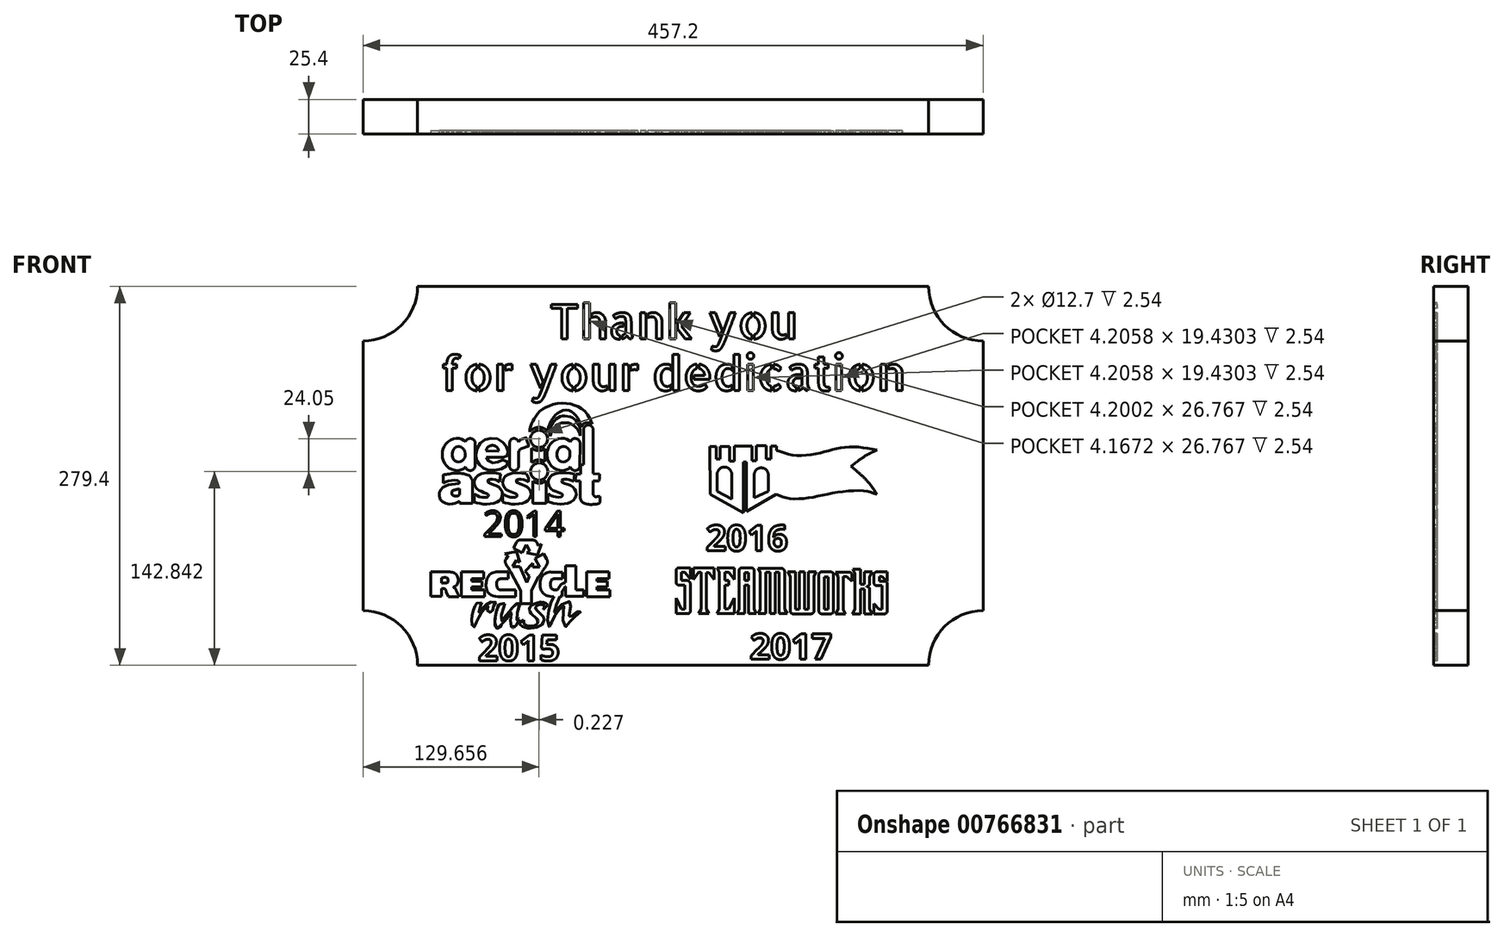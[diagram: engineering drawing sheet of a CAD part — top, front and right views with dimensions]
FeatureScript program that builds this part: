
annotation { "Feature Type Name" : "Feature", "Feature Type Description" : "" }
export const myFeature = defineFeature(function(context is Context, id is Id, definition is map)
    precondition{}
    {
        {
            var Q0;
            Q0=qCreatedBy(makeId("Front.planeOp"),FACE);
            var sketch = newSketch(context, id + "F0", { "sketchPlane" : qUnion([Q0])});
            skLineSegment(sketch, "E0", {"start": v(-457.2, -40.21) * mm, "end": v(-457.2, -239.19) * mm});
            skLineSegment(sketch, "E1", {"start": v(-416.99, -279.4) * mm, "end": v(-40.21, -279.4) * mm});
            skLineSegment(sketch, "E2", {"start": v(0, -239.19) * mm, "end": v(0, -40.21) * mm});
            skLineSegment(sketch, "E3", {"start": v(-40.21, 0) * mm, "end": v(-416.99, 0) * mm});
            skArc(sketch, "E4", {"start": v(-457.2, -40.21) * mm, "mid": v(-428.77, -28.43) * mm, "end": v(-416.99, 0) * mm});
            skLineSegment(sketch, "E5", {"start": v(-228.6, 0) * mm, "end": v(-228.6, -279.4) * mm, "construction": true});
            skLineSegment(sketch, "E6", {"start": v(-457.2, -139.7) * mm, "end": v(0, -139.7) * mm, "construction": true});
            skArc(sketch, "E7.MirrorC", {"start": v(0, -40.21) * mm, "mid": v(-28.43, -28.43) * mm, "end": v(-40.21, 0) * mm});
            skLineSegment(sketch, "E8.MirrorCS", {"start": v(0, -139.7) * mm, "end": v(-457.2, -139.7) * mm, "construction": true});
            skArc(sketch, "E9.MirrorC", {"start": v(-457.2, -239.19) * mm, "mid": v(-428.77, -250.97) * mm, "end": v(-416.99, -279.4) * mm});
            skArc(sketch, "E10.MirrorC", {"start": v(0, -239.19) * mm, "mid": v(-28.43, -250.97) * mm, "end": v(-40.21, -279.4) * mm});
            skSolve(sketch);
        }
        {
            var Q0;
            Q0 = qSketchRegion(id + "F0", true);
            extrude(context, id + "F1", {"entities" : qUnion([Q0]), "depth" : 25.4 * mm, "offsetDistance" : 25.4 * mm});
        }
        {
            var Q0;
            Q0=makeQuery(id+"F1.opExtrude","CAP_FACE",FACE,{"disambiguationData":[OSD([sQuery(id+"F0.wireOp",EDGE,"E0"),sQuery(id+"F0.wireOp",EDGE,"E1"),sQuery(id+"F0.wireOp",EDGE,"E2"),sQuery(id+"F0.wireOp",EDGE,"E3")])],"isStart":false});
            var sketch = newSketch(context, id + "F2", { "sketchPlane" : qUnion([Q0])});
            skFitSpline(sketch, "E11", {"points": [v(-381.64, -114.6) * mm, v(-382.84, -113.47) * mm, v(-384.8, -112.4) * mm, v(-387.44, -111.9) * mm, v(-391.03, -112.52) * mm, v(-394.34, -114.32) * mm, v(-396.64, -116.84) * mm, v(-398.2, -119.8) * mm, v(-398.71, -122.28) * mm, v(-398.65, -125.7) * mm, v(-398.15, -128.16) * mm, v(-396.47, -131.25) * mm, v(-393.66, -133.94) * mm, v(-390.64, -135.45) * mm, v(-386.83, -135.73) * mm, v(-383.74, -134.83) * mm, v(-381.61, -133.04) * mm, v(-379.2, -127.1) * mm], "startDerivative": vector(-26.95, 27.22) * mm, "endDerivative": vector(26.9, 83.07) * mm});
            skArc(sketch, "E12.0.endCap", {"start": v(-374.66, -132.37) * mm, "mid": v(-377.83, -135.83) * mm, "end": v(-381.62, -133.06) * mm});
            skLineSegment(sketch, "E12.0.left", {"start": v(-374.49, -115.92) * mm, "end": v(-374.66, -132.37) * mm});
            skArc(sketch, "E13", {"start": v(-374.49, -115.92) * mm, "mid": v(-377.5, -112.25) * mm, "end": v(-381.64, -114.6) * mm});
            skFitSpline(sketch, "E14", {"points": [v(-387.35, -118.18) * mm, v(-388.71, -118.55) * mm, v(-390.5, -120.1) * mm, v(-391.38, -122.82) * mm, v(-391.33, -125.68) * mm, v(-390.36, -128) * mm, v(-388.57, -129.22) * mm, v(-386.19, -129.42) * mm, v(-383.8, -128.3) * mm, v(-382.45, -126.65) * mm, v(-381.87, -124.26) * mm, v(-382.35, -120.93) * mm, v(-383.66, -119.23) * mm, v(-385.9, -118.26) * mm, v(-387.35, -118.18) * mm]});
            skLineSegment(sketch, "E15", {"start": v(-366.5, -121.42) * mm, "end": v(-357.25, -121.52) * mm});
            skArc(sketch, "E16", {"start": v(-357.25, -121.52) * mm, "mid": v(-361.83, -117.3) * mm, "end": v(-366.5, -121.42) * mm});
            skLineSegment(sketch, "E17", {"start": v(-366.3, -126.1) * mm, "end": v(-353.65, -126.1) * mm});
            skFitSpline(sketch, "E18", {"points": [v(-353.65, -126.1) * mm, v(-351.29, -125.6) * mm, v(-350.5, -124.26) * mm, v(-350.32, -121.14) * mm, v(-351.15, -118.92) * mm, v(-352.54, -116.7) * mm, v(-354.94, -114.3) * mm, v(-358.36, -112.36) * mm, v(-362.43, -112) * mm, v(-366.58, -112.92) * mm, v(-369.54, -114.58) * mm, v(-372.13, -117.35) * mm, v(-373.6, -121.14) * mm, v(-374.01, -124.8) * mm, v(-373.49, -127.83) * mm, v(-371.99, -130.8) * mm, v(-370, -132.86) * mm, v(-367.62, -134.4) * mm, v(-364.3, -135.57) * mm, v(-359.6, -135.7) * mm, v(-355.24, -134.72) * mm, v(-351.99, -132.9) * mm, v(-350.55, -131.34) * mm, v(-350.81, -129.12) * mm, v(-353.65, -127.95) * mm, v(-356.55, -129) * mm, v(-359.22, -130.03) * mm, v(-362.02, -130.1) * mm, v(-364.3, -129.06) * mm, v(-365.67, -127.75) * mm, v(-366.3, -126.1) * mm], "startDerivative": vector(116.89, 0) * mm, "endDerivative": vector(-21.57, 62.43) * mm});
            skArc(sketch, "E19.0.startCap", {"start": v(-349.14, -115.47) * mm, "mid": v(-346.25, -112.2) * mm, "end": v(-342.64, -114.66) * mm});
            skArc(sketch, "E19.0.endCap", {"start": v(-342.54, -132.58) * mm, "mid": v(-345.84, -135.88) * mm, "end": v(-349.14, -132.58) * mm});
            skLineSegment(sketch, "E19.0.left", {"start": v(-342.54, -122.14) * mm, "end": v(-342.54, -132.58) * mm});
            skLineSegment(sketch, "E19.0.right", {"start": v(-349.14, -115.47) * mm, "end": v(-349.14, -132.58) * mm});
            skFitSpline(sketch, "E20", {"points": [v(-342.64, -114.66) * mm, v(-340.58, -112.8) * mm, v(-338.46, -112.1) * mm, v(-336.5, -111.86) * mm, v(-336.5, -113.74) * mm, v(-335, -117.27) * mm, v(-335.4, -117.98) * mm, v(-336.81, -118.37) * mm, v(-338.54, -118.92) * mm, v(-341.05, -119.86) * mm, v(-342.54, -122.14) * mm], "startDerivative": vector(17.8, 19.08) * mm, "endDerivative": vector(-10.39, -23.26) * mm});
            skCircle(sketch, "E21", {"center": v(-327.54, -112.5) * mm, "radius": 6.35 * mm});
            skArc(sketch, "E22", {"start": v(-332.85, -119.24) * mm, "mid": v(-328.08, -121.06) * mm, "end": v(-323.11, -119.84) * mm});
            skFitSpline(sketch, "E23", {"points": [v(-334.25, -107.17) * mm, v(-334.19, -104.93) * mm, v(-333.33, -102.43) * mm, v(-332.32, -99.94) * mm, v(-331.24, -97.7) * mm, v(-329.36, -95.3) * mm, v(-327.13, -92.47) * mm, v(-323.79, -89.99) * mm, v(-319.93, -88.1) * mm, v(-313.59, -86.39) * mm, v(-306.99, -86.39) * mm, v(-301.59, -87.41) * mm, v(-296.7, -89.9) * mm, v(-292.24, -93.67) * mm, v(-288.04, -101.47) * mm], "startDerivative": vector(-2.37, 43.6) * mm, "endDerivative": vector(38.1, -85.11) * mm});
            skFitSpline(sketch, "E24", {"points": [v(-288.04, -101.47) * mm, v(-290.36, -100.61) * mm, v(-292.59, -100.7) * mm, v(-294.99, -101.47) * mm, v(-296.2, -103.49) * mm, v(-297.5, -99.8) * mm, v(-299.73, -95.99) * mm, v(-302.19, -93.41) * mm, v(-305.1, -91.61) * mm, v(-308.96, -91.44) * mm, v(-313.07, -93.07) * mm, v(-316.5, -96.16) * mm, v(-319.59, -101.47) * mm, v(-321.36, -106.57) * mm], "startDerivative": vector(-37.27, 17.9) * mm, "endDerivative": vector(-16.52, -54.42) * mm});
            skCircle(sketch, "E25", {"center": v(-327.32, -136.56) * mm, "radius": 6.35 * mm});
            skArc(sketch, "E26", {"start": v(-332.15, -143.64) * mm, "mid": v(-327.13, -145.13) * mm, "end": v(-322.18, -143.42) * mm});
            skLineSegment(sketch, "E27", {"start": v(-332.85, -119.24) * mm, "end": v(-332.85, -130.01) * mm});
            skLineSegment(sketch, "E28", {"start": v(-323.11, -119.84) * mm, "end": v(-323.11, -129.09) * mm});
            skArc(sketch, "E29.trimOffspring", {"start": v(-321.36, -106.57) * mm, "mid": v(-327.94, -103.94) * mm, "end": v(-334.25, -107.17) * mm});
            skLineSegment(sketch, "E30", {"start": v(-332.15, -143.64) * mm, "end": v(-332.15, -159.4) * mm});
            skLineSegment(sketch, "E31", {"start": v(-331.52, -160.03) * mm, "end": v(-322.83, -160.12) * mm});
            skLineSegment(sketch, "E32", {"start": v(-322.18, -159.49) * mm, "end": v(-322.18, -143.42) * mm});
            skPoint(sketch, "E33.visualSharp", {"position": v(-332.15, -160.02) * mm});
            skArc(sketch, "E33.filletArc", {"start": v(-332.15, -159.4) * mm, "mid": v(-331.96, -159.84) * mm, "end": v(-331.52, -160.03) * mm});
            skPoint(sketch, "E34.visualSharp", {"position": v(-322.18, -160.13) * mm});
            skArc(sketch, "E34.filletArc", {"start": v(-322.83, -160.12) * mm, "mid": v(-322.37, -159.94) * mm, "end": v(-322.18, -159.49) * mm});
            skArc(sketch, "E35.trimOffspring", {"start": v(-323.11, -129.09) * mm, "mid": v(-328.13, -128.02) * mm, "end": v(-332.85, -130.01) * mm});
            skFitSpline(sketch, "E36", {"points": [v(-319.18, -110.39) * mm, v(-319.6, -107.16) * mm, v(-318.85, -103.4) * mm, v(-316.92, -100.19) * mm, v(-314.67, -97.72) * mm, v(-311.66, -95.9) * mm, v(-308, -95.57) * mm, v(-303.93, -96.32) * mm, v(-301.25, -97.93) * mm, v(-299.2, -100.5) * mm, v(-297.27, -104.8) * mm, v(-297.17, -110.17) * mm], "startDerivative": vector(-7.7, 37.27) * mm, "endDerivative": vector(-3.75, -50.87) * mm});
            skFitSpline(sketch, "E37", {"points": [v(-297.17, -110.17) * mm, v(-298.35, -106.52) * mm, v(-299.74, -104.48) * mm, v(-302.21, -102.33) * mm, v(-305.22, -100.83) * mm, v(-308.55, -100.61) * mm, v(-311.88, -101.04) * mm, v(-316.06, -103.84) * mm, v(-317.89, -106.63) * mm, v(-319.18, -110.39) * mm], "startDerivative": vector(-9.3, 34.22) * mm, "endDerivative": vector(-10.28, -33.52) * mm});
            skFitSpline(sketch, "E38", {"points": [v(-304.35, -114.6) * mm, v(-305.55, -113.47) * mm, v(-307.5, -112.4) * mm, v(-310.14, -111.9) * mm, v(-313.73, -112.52) * mm, v(-317.04, -114.32) * mm, v(-319.34, -116.84) * mm, v(-320.9, -119.8) * mm, v(-321.41, -122.28) * mm, v(-321.36, -125.7) * mm, v(-320.85, -128.16) * mm, v(-319.17, -131.25) * mm, v(-316.37, -133.94) * mm, v(-313.34, -135.45) * mm, v(-309.53, -135.73) * mm, v(-306.44, -134.83) * mm, v(-304.31, -133.04) * mm, v(-301.9, -127.1) * mm], "startDerivative": vector(-26.95, 27.22) * mm, "endDerivative": vector(26.9, 83.07) * mm});
            skArc(sketch, "E39.0.endCap", {"start": v(-297.37, -132.37) * mm, "mid": v(-300.54, -135.83) * mm, "end": v(-304.33, -133.06) * mm});
            skLineSegment(sketch, "E39.0.left", {"start": v(-297.2, -115.92) * mm, "end": v(-297.37, -132.37) * mm});
            skArc(sketch, "E40", {"start": v(-297.2, -115.92) * mm, "mid": v(-300.21, -112.25) * mm, "end": v(-304.35, -114.6) * mm});
            skFitSpline(sketch, "E41", {"points": [v(-310.05, -118.18) * mm, v(-311.41, -118.55) * mm, v(-313.2, -120.1) * mm, v(-314.08, -122.82) * mm, v(-314.03, -125.68) * mm, v(-313.06, -128) * mm, v(-311.27, -129.22) * mm, v(-308.9, -129.42) * mm, v(-306.51, -128.3) * mm, v(-305.15, -126.65) * mm, v(-304.57, -124.26) * mm, v(-305.06, -120.93) * mm, v(-306.37, -119.23) * mm, v(-308.6, -118.26) * mm, v(-310.05, -118.18) * mm]});
            skLineSegment(sketch, "E42", {"start": v(-287.66, -105.14) * mm, "end": v(-287.66, -138.24) * mm});
            skLineSegment(sketch, "E43", {"start": v(-287.66, -138.24) * mm, "end": v(-282.77, -138.3) * mm});
            skLineSegment(sketch, "E44", {"start": v(-282.77, -138.3) * mm, "end": v(-282.77, -141.77) * mm});
            skLineSegment(sketch, "E45", {"start": v(-282.77, -141.77) * mm, "end": v(-283.27, -143.55) * mm});
            skLineSegment(sketch, "E46", {"start": v(-283.27, -143.55) * mm, "end": v(-287.52, -143.5) * mm});
            skLineSegment(sketch, "E47", {"start": v(-287.52, -143.5) * mm, "end": v(-287.52, -153.4) * mm});
            skFitSpline(sketch, "E48", {"points": [v(-287.52, -153.4) * mm, v(-286.84, -154.57) * mm, v(-285.76, -155.2) * mm, v(-283.67, -154.8) * mm], "startDerivative": vector(1.89, -4.02) * mm, "endDerivative": vector(5.77, 1.79) * mm});
            skLineSegment(sketch, "E49", {"start": v(-283.67, -154.8) * mm, "end": v(-282.48, -154.8) * mm});
            skLineSegment(sketch, "E50", {"start": v(-282.48, -154.8) * mm, "end": v(-282.48, -157.52) * mm});
            skFitSpline(sketch, "E51", {"points": [v(-282.48, -157.52) * mm, v(-282.48, -159.3) * mm, v(-283.82, -160.44) * mm, v(-286.32, -160.54) * mm, v(-289.34, -160.96) * mm, v(-291.43, -160.65) * mm, v(-293.82, -160.02) * mm, v(-296.74, -157.52) * mm, v(-297.16, -154.08) * mm, v(-297.05, -143.67) * mm], "startDerivative": vector(3.8, -22.5) * mm, "endDerivative": vector(0.14, 58.8) * mm});
            skLineSegment(sketch, "E52", {"start": v(-297.05, -143.67) * mm, "end": v(-300.6, -143.67) * mm});
            skLineSegment(sketch, "E53", {"start": v(-300.6, -143.67) * mm, "end": v(-300.13, -138.49) * mm});
            skLineSegment(sketch, "E54", {"start": v(-300.13, -138.49) * mm, "end": v(-296.71, -138.49) * mm});
            skLineSegment(sketch, "E55", {"start": v(-296.71, -138.49) * mm, "end": v(-296.71, -132.98) * mm});
            skArc(sketch, "E56", {"start": v(-295.25, -131.44) * mm, "mid": v(-296.29, -131.92) * mm, "end": v(-296.71, -132.98) * mm});
            skLineSegment(sketch, "E57", {"start": v(-295.25, -131.44) * mm, "end": v(-294.5, -131.4) * mm});
            skLineSegment(sketch, "E58", {"start": v(-294.5, -131.4) * mm, "end": v(-294.5, -105.14) * mm});
            skArc(sketch, "E59", {"start": v(-287.66, -105.14) * mm, "mid": v(-291.08, -102.23) * mm, "end": v(-294.5, -105.14) * mm});
            skLineSegment(sketch, "E60", {"start": v(-398.2, -144.95) * mm, "end": v(-398.2, -139.97) * mm});
            skFitSpline(sketch, "E61", {"points": [v(-398.2, -139.97) * mm, v(-398.2, -139.26) * mm, v(-395.87, -138.75) * mm, v(-392.12, -138.03) * mm, v(-387.72, -137.9) * mm, v(-384.23, -137.97) * mm, v(-381.32, -138.62) * mm, v(-378.47, -139.97) * mm, v(-376.61, -143.08) * mm], "startDerivative": vector(-3.73, 12.95) * mm, "endDerivative": vector(10.17, -25.55) * mm});
            skLineSegment(sketch, "E62", {"start": v(-376.61, -143.08) * mm, "end": v(-376.61, -160.06) * mm});
            skLineSegment(sketch, "E63", {"start": v(-376.61, -160.06) * mm, "end": v(-386.1, -160.06) * mm});
            skLineSegment(sketch, "E64", {"start": v(-386.1, -160.06) * mm, "end": v(-386.1, -158.47) * mm});
            skFitSpline(sketch, "E65", {"points": [v(-386.1, -158.47) * mm, v(-388.17, -159.47) * mm, v(-389.68, -160) * mm, v(-391.5, -160.44) * mm, v(-395.28, -160.28) * mm, v(-399.09, -158.47) * mm, v(-400.85, -155.44) * mm, v(-400.85, -151.7) * mm, v(-399.3, -149.22) * mm, v(-396.75, -147.39) * mm, v(-393.67, -146.36) * mm, v(-390, -145.78) * mm, v(-386.1, -145.12) * mm, v(-386.1, -144.31) * mm, v(-387.23, -143.29) * mm, v(-390.23, -143.07) * mm, v(-392.94, -143.43) * mm, v(-395.72, -144.1) * mm, v(-398.2, -144.95) * mm], "startDerivative": vector(-42.37, -21.84) * mm, "endDerivative": vector(-44.8, -16.78) * mm});
            skLineSegment(sketch, "E66", {"start": v(-386.13, -149.22) * mm, "end": v(-386.13, -153.69) * mm});
            skFitSpline(sketch, "E67", {"points": [v(-386.13, -153.69) * mm, v(-387.15, -154.35) * mm, v(-388.4, -154.71) * mm, v(-390, -154.64) * mm, v(-391.47, -153.69) * mm, v(-391.86, -152.33) * mm, v(-391.42, -150.88) * mm, v(-390, -150.17) * mm, v(-388.03, -149.8) * mm, v(-386.13, -149.22) * mm], "startDerivative": vector(-10.07, -7.34) * mm, "endDerivative": vector(14.7, 5.52) * mm});
            skLineSegment(sketch, "E68", {"start": v(-355.88, -138.5) * mm, "end": v(-356.38, -144.04) * mm});
            skLineSegment(sketch, "E69", {"start": v(-375.3, -153.7) * mm, "end": v(-375.35, -158.95) * mm});
            skFitSpline(sketch, "E70", {"points": [v(-375.3, -153.7) * mm, v(-375.01, -153.46) * mm, v(-374.4, -153.36) * mm, v(-373.52, -154.01) * mm, v(-371.66, -154.98) * mm, v(-370.04, -155.4) * mm, v(-368.18, -155.71) * mm, v(-366.04, -155.58) * mm, v(-365.07, -155.08) * mm, v(-364.6, -154.25) * mm, v(-364.97, -153.33) * mm, v(-365.7, -152.89) * mm, v(-366.98, -152.39) * mm, v(-368.73, -151.73) * mm, v(-370.12, -151.16) * mm, v(-372.19, -150.3) * mm, v(-373.73, -148.8) * mm, v(-374.88, -146.84) * mm, v(-375.3, -144.62) * mm, v(-374.45, -141.62) * mm, v(-372.3, -139.3) * mm, v(-368.1, -137.83) * mm, v(-360.72, -137.7) * mm, v(-355.88, -138.5) * mm], "startDerivative": vector(12.94, 13.12) * mm, "endDerivative": vector(65.15, -13.59) * mm});
            skFitSpline(sketch, "E71", {"points": [v(-356.38, -144.04) * mm, v(-357.93, -143.41) * mm, v(-359.6, -142.7) * mm, v(-361.14, -142.36) * mm, v(-363.24, -142.36) * mm, v(-364.88, -142.89) * mm, v(-365.4, -144.04) * mm, v(-364.3, -145.05) * mm, v(-361.47, -146.04) * mm, v(-359.6, -146.69) * mm, v(-357.4, -147.8) * mm, v(-355.88, -149.38) * mm, v(-354.78, -151.16) * mm, v(-354.52, -154.17) * mm, v(-355.88, -157.2) * mm, v(-357.66, -158.7) * mm, v(-360.16, -159.88) * mm, v(-363.77, -160.54) * mm, v(-367.18, -160.8) * mm, v(-370.6, -160.21) * mm, v(-373.15, -159.69) * mm, v(-375.35, -158.95) * mm], "startDerivative": vector(-38, 14.53) * mm, "endDerivative": vector(-45.82, 17.03) * mm});
            skLineSegment(sketch, "E72", {"start": v(-335.08, -141.26) * mm, "end": v(-335.33, -144.03) * mm});
            skLineSegment(sketch, "E73", {"start": v(-354.25, -153.7) * mm, "end": v(-354.3, -158.95) * mm});
            skFitSpline(sketch, "E74", {"points": [v(-354.25, -153.7) * mm, v(-353.96, -153.46) * mm, v(-353.36, -153.36) * mm, v(-352.47, -154.01) * mm, v(-350.61, -154.98) * mm, v(-349, -155.4) * mm, v(-347.14, -155.71) * mm, v(-345, -155.58) * mm, v(-344.02, -155.08) * mm, v(-343.55, -154.25) * mm, v(-343.92, -153.33) * mm, v(-344.65, -152.89) * mm, v(-345.93, -152.39) * mm, v(-347.68, -151.73) * mm, v(-349.07, -151.16) * mm, v(-351.14, -150.3) * mm, v(-352.68, -148.8) * mm, v(-353.83, -146.84) * mm, v(-354.25, -144.62) * mm, v(-353.4, -141.62) * mm, v(-351.26, -139.3) * mm, v(-347.04, -137.83) * mm, v(-339.67, -137.7) * mm, v(-334.83, -138.5) * mm], "startDerivative": vector(12.94, 13.12) * mm, "endDerivative": vector(65.15, -13.59) * mm});
            skFitSpline(sketch, "E75", {"points": [v(-335.33, -144.03) * mm, v(-336.88, -143.41) * mm, v(-338.56, -142.7) * mm, v(-340.1, -142.36) * mm, v(-342.2, -142.36) * mm, v(-343.83, -142.89) * mm, v(-344.36, -144.03) * mm, v(-343.25, -145.05) * mm, v(-340.42, -146.04) * mm, v(-338.56, -146.69) * mm, v(-336.35, -147.8) * mm, v(-334.83, -149.38) * mm, v(-333.73, -151.16) * mm, v(-333.47, -154.17) * mm, v(-334.83, -157.2) * mm, v(-336.62, -158.7) * mm, v(-339.1, -159.88) * mm, v(-342.72, -160.54) * mm, v(-346.13, -160.8) * mm, v(-349.54, -160.21) * mm, v(-352.1, -159.69) * mm, v(-354.3, -158.95) * mm], "startDerivative": vector(-38, 14.53) * mm, "endDerivative": vector(-45.82, 17.03) * mm});
            skLineSegment(sketch, "E76", {"start": v(-335.08, -141.26) * mm, "end": v(-336.71, -138.11) * mm});
            skPoint(sketch, "E77.orphan", {"position": v(-334.83, -138.49) * mm});
            skLineSegment(sketch, "E78", {"start": v(-301.37, -138.37) * mm, "end": v(-301.87, -143.92) * mm});
            skLineSegment(sketch, "E79", {"start": v(-320.8, -153.58) * mm, "end": v(-320.85, -158.84) * mm});
            skFitSpline(sketch, "E80", {"points": [v(-320.8, -153.58) * mm, v(-320.5, -153.34) * mm, v(-319.9, -153.24) * mm, v(-319.02, -153.9) * mm, v(-317.16, -154.86) * mm, v(-315.54, -155.28) * mm, v(-313.68, -155.6) * mm, v(-311.53, -155.46) * mm, v(-310.57, -154.97) * mm, v(-310.1, -154.13) * mm, v(-310.46, -153.21) * mm, v(-311.2, -152.77) * mm, v(-312.48, -152.27) * mm, v(-314.23, -151.62) * mm, v(-315.61, -151.04) * mm, v(-317.68, -150.18) * mm, v(-319.22, -148.69) * mm, v(-320.38, -146.73) * mm, v(-320.8, -144.5) * mm, v(-319.95, -141.5) * mm, v(-317.8, -139.18) * mm, v(-313.59, -137.72) * mm, v(-306.22, -137.58) * mm, v(-301.37, -138.37) * mm], "startDerivative": vector(12.94, 13.12) * mm, "endDerivative": vector(65.15, -13.59) * mm});
            skFitSpline(sketch, "E81", {"points": [v(-301.87, -143.92) * mm, v(-303.42, -143.3) * mm, v(-305.1, -142.58) * mm, v(-306.64, -142.25) * mm, v(-308.74, -142.25) * mm, v(-310.38, -142.77) * mm, v(-310.9, -143.92) * mm, v(-309.8, -144.94) * mm, v(-306.97, -145.92) * mm, v(-305.1, -146.57) * mm, v(-302.9, -147.7) * mm, v(-301.37, -149.27) * mm, v(-300.27, -151.04) * mm, v(-300.01, -154.06) * mm, v(-301.37, -157.08) * mm, v(-303.16, -158.59) * mm, v(-305.65, -159.77) * mm, v(-309.26, -160.42) * mm, v(-312.68, -160.69) * mm, v(-316.09, -160.1) * mm, v(-318.65, -159.57) * mm, v(-320.85, -158.84) * mm], "startDerivative": vector(-38, 14.53) * mm, "endDerivative": vector(-45.82, 17.03) * mm});
            skLineSegment(sketch, "E82", {"start": v(-384.8, -210.42) * mm, "end": v(-384.8, -228.88) * mm});
            skLineSegment(sketch, "E83", {"start": v(-384.8, -228.88) * mm, "end": v(-367.7, -228.88) * mm});
            skLineSegment(sketch, "E84", {"start": v(-367.7, -228.88) * mm, "end": v(-367.7, -223.75) * mm});
            skLineSegment(sketch, "E85", {"start": v(-367.7, -223.75) * mm, "end": v(-377.03, -223.75) * mm});
            skLineSegment(sketch, "E86", {"start": v(-377.03, -223.75) * mm, "end": v(-377.03, -221.76) * mm});
            skLineSegment(sketch, "E87", {"start": v(-377.03, -221.76) * mm, "end": v(-369.54, -221.76) * mm});
            skLineSegment(sketch, "E88", {"start": v(-369.54, -221.76) * mm, "end": v(-369.54, -217.59) * mm});
            skLineSegment(sketch, "E89", {"start": v(-369.54, -217.59) * mm, "end": v(-377.1, -217.59) * mm});
            skLineSegment(sketch, "E90", {"start": v(-377.1, -217.59) * mm, "end": v(-377.1, -215.6) * mm});
            skLineSegment(sketch, "E91", {"start": v(-377.1, -215.6) * mm, "end": v(-368.11, -215.6) * mm});
            skLineSegment(sketch, "E92", {"start": v(-368.11, -215.6) * mm, "end": v(-368.11, -210.42) * mm});
            skLineSegment(sketch, "E93", {"start": v(-368.11, -210.42) * mm, "end": v(-384.8, -210.42) * mm});
            skLineSegment(sketch, "E94.bottom", {"start": v(-407.17, -210.59) * mm, "end": v(-399.46, -210.59) * mm});
            skLineSegment(sketch, "E94.top", {"start": v(-407.17, -228.77) * mm, "end": v(-399.46, -228.77) * mm});
            skLineSegment(sketch, "E94.left", {"start": v(-407.17, -210.59) * mm, "end": v(-407.17, -228.77) * mm});
            skLineSegment(sketch, "E94.right", {"start": v(-399.46, -214.93) * mm, "end": v(-399.46, -218.85) * mm});
            skFitSpline(sketch, "E95", {"points": [v(-399.46, -210.59) * mm, v(-394.1, -210.59) * mm, v(-391.95, -210.85) * mm, v(-390.32, -211.33) * mm, v(-388.8, -212.13) * mm, v(-387.86, -213.28) * mm, v(-387.32, -214.43) * mm, v(-387.1, -216.02) * mm, v(-387.13, -217.71) * mm, v(-387.52, -219.17) * mm, v(-388.32, -220.4) * mm, v(-389.7, -221.48) * mm, v(-390.8, -221.9) * mm], "startDerivative": vector(42.38, 0.73) * mm, "endDerivative": vector(-16, -4.77) * mm});
            skFitSpline(sketch, "E96", {"points": [v(-390.8, -221.9) * mm, v(-390.05, -222.32) * mm, v(-389.1, -223.07) * mm, v(-388.37, -224.46) * mm, v(-387.86, -225.6) * mm, v(-386.56, -228.88) * mm], "startDerivative": vector(4.88, -2.66) * mm, "endDerivative": vector(4.84, -12.6) * mm});
            skLineSegment(sketch, "E97", {"start": v(-386.56, -228.88) * mm, "end": v(-394.38, -228.88) * mm});
            skLineSegment(sketch, "E98", {"start": v(-394.38, -228.88) * mm, "end": v(-395.7, -225.57) * mm});
            skFitSpline(sketch, "E99", {"points": [v(-395.7, -225.57) * mm, v(-396.16, -224.31) * mm, v(-396.58, -223.37) * mm, v(-397.36, -222.89) * mm, v(-399.1, -222.82) * mm, v(-399.46, -222.82) * mm], "startDerivative": vector(-2.08, 5.74) * mm, "endDerivative": vector(-2.94, 0.06) * mm});
            skFitSpline(sketch, "E100", {"points": [v(-399.46, -214.93) * mm, v(-395.7, -214.85) * mm, v(-394.76, -215.6) * mm, v(-394.44, -216.61) * mm, v(-394.65, -217.89) * mm, v(-395.12, -218.5) * mm, v(-395.7, -218.7) * mm, v(-396.91, -218.85) * mm, v(-398.6, -218.82) * mm, v(-399.46, -218.85) * mm], "startDerivative": vector(23.7, 2.7) * mm, "endDerivative": vector(-9.58, -0.43) * mm});
            skLineSegment(sketch, "E101.trimOffspring", {"start": v(-399.46, -222.82) * mm, "end": v(-399.46, -228.77) * mm});
            skLineSegment(sketch, "E102.bottom", {"start": v(-308.04, -206.21) * mm, "end": v(-300.29, -206.21) * mm});
            skLineSegment(sketch, "E102.top", {"start": v(-308.04, -228.67) * mm, "end": v(-300.29, -228.67) * mm});
            skLineSegment(sketch, "E102.left", {"start": v(-308.04, -206.21) * mm, "end": v(-308.04, -218.48) * mm});
            skLineSegment(sketch, "E102.right", {"start": v(-300.29, -206.21) * mm, "end": v(-300.29, -223.86) * mm});
            skLineSegment(sketch, "E103", {"start": v(-300.29, -228.67) * mm, "end": v(-294.59, -228.67) * mm});
            skLineSegment(sketch, "E104", {"start": v(-294.59, -228.67) * mm, "end": v(-294.59, -223.86) * mm});
            skLineSegment(sketch, "E105", {"start": v(-294.59, -223.86) * mm, "end": v(-300.29, -223.86) * mm});
            skLineSegment(sketch, "E106", {"start": v(-310.4, -225.02) * mm, "end": v(-310.4, -228.68) * mm});
            skLineSegment(sketch, "E107", {"start": v(-310.4, -228.68) * mm, "end": v(-312.06, -228.68) * mm});
            skFitSpline(sketch, "E108", {"points": [v(-310.4, -225.02) * mm, v(-309.67, -223.94) * mm, v(-308.86, -222.71) * mm, v(-308.04, -221.21) * mm], "startDerivative": vector(2.32, 3.42) * mm, "endDerivative": vector(2.26, 4.32) * mm});
            skFitSpline(sketch, "E109", {"points": [v(-308.04, -218.48) * mm, v(-309.75, -219.01) * mm, v(-310.94, -219.7) * mm, v(-312.17, -221.17) * mm, v(-313.9, -223.8) * mm], "startDerivative": vector(-7.59, -2.16) * mm, "endDerivative": vector(-5.73, -8.86) * mm});
            skFitSpline(sketch, "E110", {"points": [v(-313.9, -223.8) * mm, v(-316.63, -223.8) * mm, v(-318.6, -222.26) * mm, v(-318.88, -219.7) * mm, v(-318.75, -217.41) * mm, v(-317.64, -216.02) * mm, v(-315, -215.6) * mm], "startDerivative": vector(-15.66, -2.03) * mm, "endDerivative": vector(16.66, 0.52) * mm});
            skLineSegment(sketch, "E111", {"start": v(-315, -215.6) * mm, "end": v(-310.27, -215.6) * mm});
            skLineSegment(sketch, "E112", {"start": v(-310.27, -215.6) * mm, "end": v(-310.27, -210.7) * mm});
            skLineSegment(sketch, "E113", {"start": v(-310.27, -210.7) * mm, "end": v(-318.35, -210.7) * mm});
            skFitSpline(sketch, "E114", {"points": [v(-318.35, -210.7) * mm, v(-319.53, -210.7) * mm, v(-322, -211.41) * mm, v(-323.74, -212.4) * mm, v(-325.37, -214.14) * mm, v(-326.25, -216.2) * mm, v(-326.65, -217.97) * mm, v(-326.57, -221.23) * mm, v(-326.14, -223.58) * mm, v(-324.6, -226.12) * mm, v(-322.88, -227.5) * mm, v(-319.58, -228.7) * mm, v(-316.41, -228.75) * mm], "startDerivative": vector(-17.73, 2.05) * mm, "endDerivative": vector(32.25, 2.73) * mm});
            skLineSegment(sketch, "E115.trimOffspring", {"start": v(-308.04, -221.21) * mm, "end": v(-308.04, -228.67) * mm});
            skLineSegment(sketch, "E116", {"start": v(-292.4, -210.42) * mm, "end": v(-292.4, -228.88) * mm});
            skLineSegment(sketch, "E117", {"start": v(-292.4, -228.88) * mm, "end": v(-275.3, -228.88) * mm});
            skLineSegment(sketch, "E118", {"start": v(-275.3, -228.88) * mm, "end": v(-275.3, -223.75) * mm});
            skLineSegment(sketch, "E119", {"start": v(-275.3, -223.75) * mm, "end": v(-284.64, -223.75) * mm});
            skLineSegment(sketch, "E120", {"start": v(-284.64, -223.75) * mm, "end": v(-284.64, -221.76) * mm});
            skLineSegment(sketch, "E121", {"start": v(-284.64, -221.76) * mm, "end": v(-277.16, -221.76) * mm});
            skLineSegment(sketch, "E122", {"start": v(-277.16, -221.76) * mm, "end": v(-277.16, -217.59) * mm});
            skLineSegment(sketch, "E123", {"start": v(-277.16, -217.59) * mm, "end": v(-284.72, -217.59) * mm});
            skLineSegment(sketch, "E124", {"start": v(-284.72, -217.59) * mm, "end": v(-284.72, -215.6) * mm});
            skLineSegment(sketch, "E125", {"start": v(-284.72, -215.6) * mm, "end": v(-275.72, -215.6) * mm});
            skLineSegment(sketch, "E126", {"start": v(-275.72, -215.6) * mm, "end": v(-275.72, -210.42) * mm});
            skLineSegment(sketch, "E127", {"start": v(-275.72, -210.42) * mm, "end": v(-292.4, -210.42) * mm});
            skLineSegment(sketch, "E128", {"start": v(-340.8, -234.15) * mm, "end": v(-332.98, -234.15) * mm});
            skLineSegment(sketch, "E129", {"start": v(-332.98, -234.15) * mm, "end": v(-332.98, -224.62) * mm});
            skLineSegment(sketch, "E130", {"start": v(-332.98, -224.62) * mm, "end": v(-327.78, -214.14) * mm});
            skLineSegment(sketch, "E131", {"start": v(-340.8, -234.15) * mm, "end": v(-340.8, -224.62) * mm});
            skLineSegment(sketch, "E132", {"start": v(-340.8, -224.62) * mm, "end": v(-348.1, -210.88) * mm});
            skLineSegment(sketch, "E133", {"start": v(-350.25, -198.44) * mm, "end": v(-352.73, -197.24) * mm});
            skLineSegment(sketch, "E134", {"start": v(-352.73, -197.24) * mm, "end": v(-344.1, -195.59) * mm});
            skLineSegment(sketch, "E135", {"start": v(-344.1, -195.59) * mm, "end": v(-341.6, -203.46) * mm});
            skLineSegment(sketch, "E136", {"start": v(-341.6, -203.46) * mm, "end": v(-343.94, -202.03) * mm});
            skLineSegment(sketch, "E137", {"start": v(-334.56, -213.83) * mm, "end": v(-337.63, -210.28) * mm});
            skLineSegment(sketch, "E138", {"start": v(-337.63, -210.28) * mm, "end": v(-332.06, -204.18) * mm});
            skLineSegment(sketch, "E139", {"start": v(-332.06, -204.18) * mm, "end": v(-332.13, -206.93) * mm});
            skLineSegment(sketch, "E140", {"start": v(-327.93, -191.5) * mm, "end": v(-325.65, -189.96) * mm});
            skLineSegment(sketch, "E141", {"start": v(-325.65, -189.96) * mm, "end": v(-328.54, -198.26) * mm});
            skLineSegment(sketch, "E142", {"start": v(-328.54, -198.26) * mm, "end": v(-336.61, -196.5) * mm});
            skLineSegment(sketch, "E143", {"start": v(-336.61, -196.5) * mm, "end": v(-334.2, -195.18) * mm});
            skLineSegment(sketch, "E144", {"start": v(-334.2, -195.18) * mm, "end": v(-336.72, -190.54) * mm});
            skLineSegment(sketch, "E145", {"start": v(-336.72, -190.54) * mm, "end": v(-340.1, -196.63) * mm});
            skLineSegment(sketch, "E146", {"start": v(-340.1, -196.63) * mm, "end": v(-346.4, -193.15) * mm});
            skLineSegment(sketch, "E147", {"start": v(-346.4, -193.15) * mm, "end": v(-343.97, -188.78) * mm});
            skFitSpline(sketch, "E148", {"points": [v(-343.97, -188.78) * mm, v(-343.08, -187.7) * mm, v(-341.18, -187.07) * mm, v(-331.09, -187.21) * mm, v(-330.8, -187.28) * mm, v(-330.12, -187.7) * mm, v(-329.21, -188.78) * mm, v(-327.93, -191.5) * mm], "startDerivative": vector(7.55, 10.2) * mm, "endDerivative": vector(7.62, -17.7) * mm});
            skLineSegment(sketch, "E149", {"start": v(-343.94, -202.03) * mm, "end": v(-346.81, -206.74) * mm});
            skLineSegment(sketch, "E150", {"start": v(-346.81, -206.74) * mm, "end": v(-341.4, -206.74) * mm});
            skLineSegment(sketch, "E151", {"start": v(-341.4, -206.74) * mm, "end": v(-336.54, -218.55) * mm});
            skLineSegment(sketch, "E152", {"start": v(-336.54, -218.55) * mm, "end": v(-334.56, -213.83) * mm});
            skLineSegment(sketch, "E153", {"start": v(-350.25, -198.44) * mm, "end": v(-351.84, -201.08) * mm});
            skFitSpline(sketch, "E154", {"points": [v(-351.84, -201.08) * mm, v(-352.26, -201.86) * mm, v(-352.4, -203.23) * mm, v(-351.84, -204.7) * mm, v(-348.1, -210.88) * mm], "startDerivative": vector(-3.02, -4.47) * mm, "endDerivative": vector(10.8, -16.46) * mm});
            skLineSegment(sketch, "E155", {"start": v(-332.13, -206.93) * mm, "end": v(-326.92, -206.93) * mm});
            skLineSegment(sketch, "E156", {"start": v(-326.92, -206.93) * mm, "end": v(-330.37, -200.57) * mm});
            skLineSegment(sketch, "E157", {"start": v(-330.37, -200.57) * mm, "end": v(-323.94, -197.07) * mm});
            skLineSegment(sketch, "E158", {"start": v(-323.94, -197.07) * mm, "end": v(-321.8, -201.01) * mm});
            skFitSpline(sketch, "E159", {"points": [v(-321.8, -201.01) * mm, v(-321.2, -202.57) * mm, v(-321.4, -204.57) * mm, v(-324, -208.73) * mm, v(-326.7, -213.1) * mm, v(-327.78, -214.14) * mm], "startDerivative": vector(4.81, -9.86) * mm, "endDerivative": vector(-7.04, -5.45) * mm});
            skLineSegment(sketch, "E160", {"start": v(-350.17, -215.7) * mm, "end": v(-350.17, -210.55) * mm});
            skLineSegment(sketch, "E161", {"start": v(-350.17, -210.55) * mm, "end": v(-357.74, -210.55) * mm});
            skLineSegment(sketch, "E162", {"start": v(-350.17, -215.7) * mm, "end": v(-355.94, -215.7) * mm});
            skLineSegment(sketch, "E163", {"start": v(-344.8, -223.79) * mm, "end": v(-344.8, -228.9) * mm});
            skLineSegment(sketch, "E164", {"start": v(-344.8, -228.9) * mm, "end": v(-357.68, -228.9) * mm});
            skLineSegment(sketch, "E165", {"start": v(-344.8, -223.79) * mm, "end": v(-355.82, -223.79) * mm});
            skFitSpline(sketch, "E166", {"points": [v(-355.82, -223.79) * mm, v(-356.71, -223.79) * mm, v(-357.65, -223.09) * mm, v(-358.34, -222) * mm, v(-358.58, -220.76) * mm, v(-358.58, -219.2) * mm, v(-358.55, -217.85) * mm, v(-358.04, -216.82) * mm, v(-357.23, -216.1) * mm, v(-355.94, -215.7) * mm], "startDerivative": vector(-9.51, -1.43) * mm, "endDerivative": vector(11.9, 2.65) * mm});
            skFitSpline(sketch, "E167", {"points": [v(-357.74, -210.55) * mm, v(-359.5, -210.66) * mm, v(-361.1, -211.1) * mm, v(-362.4, -211.53) * mm, v(-363.23, -212.1) * mm, v(-364.42, -213.27) * mm, v(-365.37, -214.68) * mm, v(-366.04, -216.1) * mm, v(-366.33, -217.86) * mm, v(-366.5, -219.08) * mm, v(-366.56, -220.76) * mm, v(-366.22, -222.77) * mm, v(-365.44, -224.9) * mm, v(-364.21, -226.4) * mm, v(-361.86, -228.08) * mm, v(-357.68, -228.9) * mm], "startDerivative": vector(-27.54, -0.28) * mm, "endDerivative": vector(44.63, -4.63) * mm});
            skFitSpline(sketch, "E168", {"points": [v(-312.06, -228.68) * mm, v(-313.57, -232.13) * mm, v(-315.26, -236.31) * mm, v(-316.31, -240.62) * mm, v(-313.83, -237.36) * mm, v(-309.12, -233.7) * mm, v(-305.99, -232.26) * mm, v(-304.35, -232.64) * mm, v(-303.63, -234.08) * mm, v(-304.1, -236.28) * mm, v(-304.88, -239.97) * mm, v(-305.29, -245.02) * mm, v(-304.47, -244.35) * mm, v(-302.95, -242.78) * mm, v(-300.79, -241) * mm, v(-298.42, -239.44) * mm, v(-297.27, -238.91) * mm, v(-296.6, -239.36) * mm, v(-296.93, -240.19) * mm, v(-299.1, -241.74) * mm, v(-301.15, -243.51) * mm, v(-302.48, -244.79) * mm, v(-304.25, -246.73) * mm, v(-306.24, -249.11) * mm, v(-307.68, -251) * mm, v(-309.24, -250.28) * mm, v(-309.85, -246.78) * mm, v(-309.8, -243.07) * mm, v(-309.24, -239.7) * mm, v(-308.6, -237.12) * mm, v(-308.78, -236.17) * mm, v(-309.7, -236.12) * mm, v(-311.36, -237.07) * mm, v(-312.99, -238.8) * mm, v(-314.61, -240.8) * mm, v(-316.04, -243.1) * mm, v(-317, -245) * mm, v(-318, -247.92) * mm, v(-318.72, -250.45) * mm, v(-319.53, -251.07) * mm, v(-320.53, -250.5) * mm, v(-321.01, -247.87) * mm, v(-321.06, -244.33) * mm, v(-320.49, -239.56) * mm, v(-319.82, -236.98) * mm, v(-318.6, -233.37) * mm, v(-317.44, -230.65) * mm, v(-316.41, -228.75) * mm], "startDerivative": vector(-58.73, -135.62) * mm, "endDerivative": vector(52.61, 93.78) * mm});
            skFitSpline(sketch, "E169", {"points": [v(-338.75, -245.98) * mm, v(-338.61, -247.45) * mm, v(-338.54, -248.76) * mm, v(-337.53, -249.84) * mm, v(-335.5, -250.65) * mm, v(-332.52, -250.58) * mm, v(-330.43, -250.1) * mm, v(-328.8, -248.9) * mm, v(-328.06, -247.13) * mm, v(-328.56, -245.62) * mm, v(-330.92, -243.47) * mm, v(-331.65, -243) * mm, v(-333.27, -241.32) * mm, v(-334.55, -239.15) * mm, v(-334.42, -236.78) * mm, v(-333, -235.43) * mm, v(-330.83, -234.01) * mm, v(-328.06, -233.13) * mm, v(-325.22, -232.86) * mm, v(-322.72, -233.4) * mm, v(-320.9, -234.89) * mm], "startDerivative": vector(5.07, -36.06) * mm, "endDerivative": vector(32.32, -32.5) * mm});
            skLineSegment(sketch, "E170", {"start": v(-320.9, -234.89) * mm, "end": v(-324.27, -238.34) * mm});
            skLineSegment(sketch, "E171", {"start": v(-338.75, -245.98) * mm, "end": v(-342.2, -248.35) * mm});
            skFitSpline(sketch, "E172", {"points": [v(-342.2, -248.35) * mm, v(-341.18, -249.64) * mm, v(-339.5, -250.85) * mm, v(-336.99, -251.8) * mm, v(-333.74, -252.07) * mm, v(-330.63, -251.8) * mm, v(-327.57, -250.77) * mm, v(-325.47, -249.45) * mm, v(-324.05, -247.45) * mm, v(-323.8, -244.77) * mm, v(-325.42, -242.53) * mm, v(-327.13, -240.85) * mm, v(-328.6, -239.29) * mm, v(-329.75, -237.73) * mm, v(-329.89, -236.24) * mm, v(-327.79, -234.96) * mm, v(-325.76, -234.62) * mm, v(-324.2, -234.84) * mm, v(-323.53, -236.24) * mm, v(-324.27, -238.34) * mm], "startDerivative": vector(20.7, -29.89) * mm, "endDerivative": vector(-19.13, -40.14) * mm});
            skFitSpline(sketch, "E173", {"points": [v(-369.9, -233.26) * mm, v(-372.52, -233.26) * mm, v(-374.1, -234.24) * mm, v(-374.75, -235.75) * mm, v(-375.6, -237.84) * mm, v(-376.32, -240.72) * mm, v(-376.9, -244.05) * mm, v(-377.04, -247) * mm, v(-376.84, -249.49) * mm, v(-375.8, -251.25) * mm, v(-374.81, -250.93) * mm, v(-373.5, -247.59) * mm, v(-371.93, -243.99) * mm, v(-370.16, -240.85) * mm, v(-368.14, -238.43) * mm, v(-365.78, -236.4) * mm, v(-365, -236) * mm, v(-365.52, -237.84) * mm, v(-365.32, -239.87) * mm, v(-364.21, -240.33) * mm, v(-361.72, -240) * mm, v(-361.6, -238.1) * mm, v(-361, -235.88) * mm, v(-359.9, -233.39) * mm, v(-359.37, -232.87) * mm, v(-363.23, -232.93) * mm, v(-366.83, -235.1) * mm, v(-369.12, -237.18) * mm, v(-371.67, -240.46) * mm, v(-371.47, -238.04) * mm, v(-370.16, -234.3) * mm, v(-369.9, -233.26) * mm]});
            skFitSpline(sketch, "E174", {"points": [v(-352.63, -233.96) * mm, v(-355.03, -234.1) * mm, v(-356.36, -234.45) * mm, v(-357.73, -235.88) * mm, v(-358.52, -238.58) * mm, v(-359.1, -241.08) * mm, v(-359.55, -243.63) * mm, v(-359.9, -245.99) * mm, v(-360.09, -248.69) * mm, v(-359.65, -250.75) * mm, v(-358.57, -252.17) * mm, v(-357, -251.83) * mm, v(-355.62, -250.26) * mm, v(-354.25, -248.44) * mm, v(-352.14, -245.84) * mm, v(-350.32, -243.39) * mm, v(-348.75, -241.42) * mm, v(-347.72, -240.1) * mm, v(-347.82, -241.57) * mm, v(-348.2, -243.83) * mm, v(-348.4, -246.97) * mm, v(-348.4, -249.28) * mm, v(-347.77, -251.39) * mm, v(-346.78, -252.37) * mm, v(-344.43, -250.46) * mm, v(-342.96, -249.03) * mm, v(-342.32, -244.66) * mm, v(-342.8, -245.3) * mm, v(-343.8, -246.14) * mm, v(-343.89, -244.12) * mm, v(-343.45, -240.64) * mm, v(-342.71, -238.18) * mm, v(-341.68, -235.19) * mm, v(-341.18, -234.15) * mm, v(-343.9, -234.15) * mm, v(-344.96, -234.78) * mm, v(-346.3, -236.17) * mm, v(-349.18, -239.73) * mm, v(-353.87, -245.53) * mm, v(-354.82, -246.54) * mm, v(-355.37, -245.76) * mm, v(-355.32, -243.7) * mm, v(-354.6, -240.23) * mm, v(-353.64, -237.22) * mm, v(-353.03, -235.32) * mm, v(-352.8, -234.7) * mm, v(-352.63, -233.96) * mm]});
            skLineSegment(sketch, "E175", {"start": v(-215.93, -207.64) * mm, "end": v(-215.93, -216.03) * mm});
            skLineSegment(sketch, "E176", {"start": v(-215.93, -216.03) * mm, "end": v(-219.96, -210.93) * mm});
            skLineSegment(sketch, "E177", {"start": v(-219.96, -210.93) * mm, "end": v(-222.38, -210.93) * mm});
            skLineSegment(sketch, "E178", {"start": v(-222.38, -210.93) * mm, "end": v(-222.38, -216.9) * mm});
            skLineSegment(sketch, "E179", {"start": v(-222.38, -216.9) * mm, "end": v(-218.53, -216.9) * mm});
            skLineSegment(sketch, "E180", {"start": v(-215.93, -219.5) * mm, "end": v(-215.93, -239.54) * mm});
            skLineSegment(sketch, "E181", {"start": v(-217.9, -241.42) * mm, "end": v(-226.41, -241.42) * mm});
            skLineSegment(sketch, "E182", {"start": v(-226.41, -241.42) * mm, "end": v(-226.41, -229.99) * mm});
            skLineSegment(sketch, "E183", {"start": v(-226.41, -229.99) * mm, "end": v(-222.5, -238) * mm});
            skLineSegment(sketch, "E184", {"start": v(-222.5, -238) * mm, "end": v(-219.9, -238) * mm});
            skLineSegment(sketch, "E185", {"start": v(-219.9, -238) * mm, "end": v(-219.9, -220.38) * mm});
            skLineSegment(sketch, "E186", {"start": v(-219.9, -220.38) * mm, "end": v(-224.3, -220.38) * mm});
            skLineSegment(sketch, "E187", {"start": v(-226.34, -218.3) * mm, "end": v(-226.34, -209.53) * mm});
            skLineSegment(sketch, "E188", {"start": v(-215.93, -207.64) * mm, "end": v(-224.46, -207.64) * mm});
            skArc(sketch, "E189", {"start": v(-224.46, -207.64) * mm, "mid": v(-225.8, -208.2) * mm, "end": v(-226.34, -209.53) * mm});
            skArc(sketch, "E190", {"start": v(-226.34, -218.3) * mm, "mid": v(-225.75, -219.75) * mm, "end": v(-224.3, -220.38) * mm});
            skArc(sketch, "E191", {"start": v(-215.93, -219.5) * mm, "mid": v(-216.7, -217.66) * mm, "end": v(-218.53, -216.9) * mm});
            skArc(sketch, "E192", {"start": v(-217.9, -241.42) * mm, "mid": v(-216.51, -240.9) * mm, "end": v(-215.93, -239.54) * mm});
            skLineSegment(sketch, "E193", {"start": v(-208, -210.98) * mm, "end": v(-208, -238.1) * mm});
            skLineSegment(sketch, "E194", {"start": v(-208, -238.1) * mm, "end": v(-209.72, -241.45) * mm});
            skLineSegment(sketch, "E195", {"start": v(-209.72, -241.45) * mm, "end": v(-202.28, -241.45) * mm});
            skLineSegment(sketch, "E196", {"start": v(-202.28, -241.45) * mm, "end": v(-204, -238.18) * mm});
            skLineSegment(sketch, "E197", {"start": v(-204, -238.18) * mm, "end": v(-204, -211.01) * mm});
            skLineSegment(sketch, "E198", {"start": v(-204, -211.01) * mm, "end": v(-202.33, -211.01) * mm});
            skLineSegment(sketch, "E199", {"start": v(-202.33, -211.01) * mm, "end": v(-198.29, -216.15) * mm});
            skLineSegment(sketch, "E200", {"start": v(-198.29, -216.15) * mm, "end": v(-198.29, -207.62) * mm});
            skLineSegment(sketch, "E201", {"start": v(-198.29, -207.62) * mm, "end": v(-213.58, -207.62) * mm});
            skLineSegment(sketch, "E202", {"start": v(-213.58, -207.62) * mm, "end": v(-213.58, -216.15) * mm});
            skLineSegment(sketch, "E203", {"start": v(-213.58, -216.15) * mm, "end": v(-209.78, -210.98) * mm});
            skLineSegment(sketch, "E204", {"start": v(-209.78, -210.98) * mm, "end": v(-208, -210.98) * mm});
            skLineSegment(sketch, "E205", {"start": v(-196.17, -207.56) * mm, "end": v(-183.5, -207.56) * mm});
            skLineSegment(sketch, "E206", {"start": v(-183.5, -207.56) * mm, "end": v(-183.5, -216.11) * mm});
            skLineSegment(sketch, "E207", {"start": v(-183.5, -216.11) * mm, "end": v(-187.6, -210.94) * mm});
            skLineSegment(sketch, "E208", {"start": v(-187.6, -210.94) * mm, "end": v(-190.37, -210.94) * mm});
            skLineSegment(sketch, "E209", {"start": v(-190.37, -210.94) * mm, "end": v(-190.37, -217) * mm});
            skLineSegment(sketch, "E210", {"start": v(-190.37, -217) * mm, "end": v(-187.62, -217) * mm});
            skLineSegment(sketch, "E211", {"start": v(-187.62, -217) * mm, "end": v(-187.55, -220.37) * mm});
            skLineSegment(sketch, "E212", {"start": v(-187.55, -220.37) * mm, "end": v(-190.3, -220.37) * mm});
            skLineSegment(sketch, "E213", {"start": v(-190.3, -220.37) * mm, "end": v(-190.3, -237.94) * mm});
            skLineSegment(sketch, "E214", {"start": v(-190.3, -237.94) * mm, "end": v(-187.6, -237.94) * mm});
            skLineSegment(sketch, "E215", {"start": v(-187.6, -237.94) * mm, "end": v(-183.5, -229.97) * mm});
            skLineSegment(sketch, "E216", {"start": v(-183.5, -229.97) * mm, "end": v(-183.5, -241.4) * mm});
            skLineSegment(sketch, "E217", {"start": v(-183.5, -241.4) * mm, "end": v(-196.12, -241.4) * mm});
            skLineSegment(sketch, "E218", {"start": v(-196.12, -241.4) * mm, "end": v(-194.41, -237.94) * mm});
            skLineSegment(sketch, "E219", {"start": v(-194.41, -237.94) * mm, "end": v(-194.41, -210.96) * mm});
            skLineSegment(sketch, "E220", {"start": v(-194.41, -210.96) * mm, "end": v(-196.17, -207.56) * mm});
            skLineSegment(sketch, "E221.bottom", {"start": v(-175.73, -211.06) * mm, "end": v(-172.83, -211.06) * mm});
            skLineSegment(sketch, "E221.top", {"start": v(-175.73, -216.95) * mm, "end": v(-172.83, -216.95) * mm});
            skLineSegment(sketch, "E221.left", {"start": v(-175.73, -211.06) * mm, "end": v(-175.73, -216.95) * mm});
            skLineSegment(sketch, "E221.right", {"start": v(-172.83, -211.06) * mm, "end": v(-172.83, -216.95) * mm});
            skLineSegment(sketch, "E222.bottom", {"start": v(-117.09, -214.27) * mm, "end": v(-114.26, -214.27) * mm});
            skLineSegment(sketch, "E222.top", {"start": v(-117.09, -238.07) * mm, "end": v(-114.26, -238.07) * mm});
            skLineSegment(sketch, "E222.left", {"start": v(-117.09, -214.27) * mm, "end": v(-117.09, -238.07) * mm});
            skLineSegment(sketch, "E222.right", {"start": v(-114.26, -214.27) * mm, "end": v(-114.26, -238.07) * mm});
            skLineSegment(sketch, "E223.top", {"start": v(-138.37, -238.07) * mm, "end": v(-135.52, -238.07) * mm});
            skLineSegment(sketch, "E223.left", {"start": v(-138.37, -210.63) * mm, "end": v(-138.37, -238.07) * mm});
            skLineSegment(sketch, "E223.right", {"start": v(-135.52, -210.63) * mm, "end": v(-135.52, -238.07) * mm});
            skLineSegment(sketch, "E224.top", {"start": v(-131.61, -238.07) * mm, "end": v(-128.8, -238.07) * mm});
            skLineSegment(sketch, "E224.left", {"start": v(-131.61, -210.63) * mm, "end": v(-131.61, -238.07) * mm});
            skLineSegment(sketch, "E224.right", {"start": v(-128.8, -210.63) * mm, "end": v(-128.8, -238.07) * mm});
            skLineSegment(sketch, "E225", {"start": v(-135.52, -210.63) * mm, "end": v(-131.61, -210.63) * mm});
            skLineSegment(sketch, "E226.bottom", {"start": v(-160.26, -210.96) * mm, "end": v(-157.25, -210.96) * mm});
            skLineSegment(sketch, "E226.left", {"start": v(-160.26, -210.96) * mm, "end": v(-160.26, -241.45) * mm});
            skLineSegment(sketch, "E226.right", {"start": v(-157.25, -210.96) * mm, "end": v(-157.25, -241.45) * mm});
            skLineSegment(sketch, "E227.top", {"start": v(-153.2, -210.96) * mm, "end": v(-150.33, -210.96) * mm});
            skLineSegment(sketch, "E227.left", {"start": v(-153.2, -241.45) * mm, "end": v(-153.2, -210.96) * mm});
            skLineSegment(sketch, "E227.right", {"start": v(-150.33, -241.45) * mm, "end": v(-150.33, -210.96) * mm});
            skLineSegment(sketch, "E228", {"start": v(-157.25, -241.45) * mm, "end": v(-153.2, -241.45) * mm});
            skLineSegment(sketch, "E229.bottom", {"start": v(-175.77, -220.43) * mm, "end": v(-172.9, -220.43) * mm});
            skLineSegment(sketch, "E229.left", {"start": v(-175.77, -220.43) * mm, "end": v(-175.77, -241.4) * mm});
            skLineSegment(sketch, "E229.right", {"start": v(-172.9, -220.43) * mm, "end": v(-172.9, -241.45) * mm});
            skLineSegment(sketch, "E230", {"start": v(-175.77, -241.4) * mm, "end": v(-181.55, -241.4) * mm});
            skLineSegment(sketch, "E231", {"start": v(-181.55, -241.4) * mm, "end": v(-179.84, -238.04) * mm});
            skLineSegment(sketch, "E232", {"start": v(-179.84, -238.04) * mm, "end": v(-179.84, -209.6) * mm});
            skLineSegment(sketch, "E233", {"start": v(-178.04, -207.64) * mm, "end": v(-170.82, -207.64) * mm});
            skLineSegment(sketch, "E234", {"start": v(-168.87, -209.34) * mm, "end": v(-168.87, -237.96) * mm});
            skLineSegment(sketch, "E235", {"start": v(-168.87, -237.96) * mm, "end": v(-167.14, -241.45) * mm});
            skLineSegment(sketch, "E236", {"start": v(-167.14, -241.45) * mm, "end": v(-172.9, -241.45) * mm});
            skArc(sketch, "E237", {"start": v(-178.04, -207.64) * mm, "mid": v(-179.37, -208.22) * mm, "end": v(-179.84, -209.6) * mm});
            skArc(sketch, "E238", {"start": v(-168.87, -209.34) * mm, "mid": v(-169.53, -208.13) * mm, "end": v(-170.82, -207.64) * mm});
            skLineSegment(sketch, "E239", {"start": v(-160.26, -241.45) * mm, "end": v(-166.1, -241.45) * mm});
            skLineSegment(sketch, "E240", {"start": v(-166.1, -241.45) * mm, "end": v(-164.3, -238.43) * mm});
            skLineSegment(sketch, "E241", {"start": v(-164.3, -238.43) * mm, "end": v(-164.3, -210.76) * mm});
            skLineSegment(sketch, "E242", {"start": v(-164.3, -210.76) * mm, "end": v(-165.85, -207.85) * mm});
            skLineSegment(sketch, "E243", {"start": v(-165.85, -207.85) * mm, "end": v(-149.45, -207.85) * mm});
            skLineSegment(sketch, "E244", {"start": v(-150.33, -241.45) * mm, "end": v(-144.37, -241.45) * mm});
            skLineSegment(sketch, "E245", {"start": v(-144.37, -241.45) * mm, "end": v(-146.36, -238.11) * mm});
            skLineSegment(sketch, "E246", {"start": v(-146.36, -238.11) * mm, "end": v(-146.36, -210.63) * mm});
            skArc(sketch, "E247", {"start": v(-146.36, -210.63) * mm, "mid": v(-147.28, -208.55) * mm, "end": v(-149.45, -207.85) * mm});
            skLineSegment(sketch, "E248", {"start": v(-138.37, -210.63) * mm, "end": v(-144, -210.63) * mm});
            skLineSegment(sketch, "E249", {"start": v(-144, -210.63) * mm, "end": v(-142.23, -213.97) * mm});
            skLineSegment(sketch, "E250", {"start": v(-142.23, -213.97) * mm, "end": v(-142.23, -239.6) * mm});
            skLineSegment(sketch, "E251", {"start": v(-140.22, -241.5) * mm, "end": v(-126.93, -241.5) * mm});
            skLineSegment(sketch, "E252", {"start": v(-124.7, -239.4) * mm, "end": v(-124.7, -213.87) * mm});
            skLineSegment(sketch, "E253", {"start": v(-124.7, -213.87) * mm, "end": v(-123.24, -210.63) * mm});
            skLineSegment(sketch, "E254", {"start": v(-123.24, -210.63) * mm, "end": v(-128.8, -210.63) * mm});
            skArc(sketch, "E255", {"start": v(-142.23, -239.6) * mm, "mid": v(-141.6, -240.95) * mm, "end": v(-140.22, -241.5) * mm});
            skArc(sketch, "E256", {"start": v(-126.93, -241.5) * mm, "mid": v(-125.37, -240.93) * mm, "end": v(-124.7, -239.4) * mm});
            skLineSegment(sketch, "E257.bottom", {"start": v(-119.16, -210.63) * mm, "end": v(-112.3, -210.63) * mm});
            skLineSegment(sketch, "E257.top", {"start": v(-119.16, -241.5) * mm, "end": v(-112.3, -241.5) * mm});
            skLineSegment(sketch, "E257.left", {"start": v(-121.07, -212.53) * mm, "end": v(-121.07, -239.6) * mm});
            skLineSegment(sketch, "E257.right", {"start": v(-110.39, -212.53) * mm, "end": v(-110.39, -239.6) * mm});
            skArc(sketch, "E258", {"start": v(-119.16, -210.63) * mm, "mid": v(-120.51, -211.18) * mm, "end": v(-121.07, -212.53) * mm});
            skArc(sketch, "E259", {"start": v(-110.39, -212.53) * mm, "mid": v(-110.95, -211.18) * mm, "end": v(-112.3, -210.63) * mm});
            skArc(sketch, "E260", {"start": v(-121.07, -239.6) * mm, "mid": v(-120.51, -240.94) * mm, "end": v(-119.16, -241.5) * mm});
            skArc(sketch, "E261", {"start": v(-112.3, -241.5) * mm, "mid": v(-110.95, -240.94) * mm, "end": v(-110.39, -239.6) * mm});
            skPoint(sketch, "E262.orphan", {"position": v(-121.07, -210.63) * mm});
            skPoint(sketch, "E263.orphan", {"position": v(-121.07, -241.5) * mm});
            skLineSegment(sketch, "E264", {"start": v(-106.94, -214.15) * mm, "end": v(-106.94, -238.14) * mm});
            skLineSegment(sketch, "E265", {"start": v(-106.94, -238.14) * mm, "end": v(-108.72, -241.5) * mm});
            skLineSegment(sketch, "E266", {"start": v(-108.72, -241.5) * mm, "end": v(-101.4, -241.5) * mm});
            skLineSegment(sketch, "E267", {"start": v(-101.4, -241.5) * mm, "end": v(-103.05, -238.35) * mm});
            skLineSegment(sketch, "E268", {"start": v(-103.05, -238.35) * mm, "end": v(-103.05, -214.1) * mm});
            skLineSegment(sketch, "E269", {"start": v(-103.05, -214.1) * mm, "end": v(-100.6, -214.1) * mm});
            skLineSegment(sketch, "E270", {"start": v(-100.6, -214.1) * mm, "end": v(-96.8, -217.43) * mm});
            skLineSegment(sketch, "E271", {"start": v(-96.8, -217.43) * mm, "end": v(-96.8, -212.69) * mm});
            skLineSegment(sketch, "E272", {"start": v(-106.94, -214.15) * mm, "end": v(-108.74, -210.78) * mm});
            skLineSegment(sketch, "E273", {"start": v(-108.74, -210.78) * mm, "end": v(-98.7, -210.78) * mm});
            skArc(sketch, "E274", {"start": v(-96.8, -212.69) * mm, "mid": v(-97.35, -211.34) * mm, "end": v(-98.7, -210.78) * mm});
            skLineSegment(sketch, "E275.bottom", {"start": v(-90.54, -223.16) * mm, "end": v(-87.56, -223.16) * mm});
            skLineSegment(sketch, "E275.left", {"start": v(-90.54, -223.16) * mm, "end": v(-90.54, -241.5) * mm});
            skLineSegment(sketch, "E275.right", {"start": v(-87.56, -223.16) * mm, "end": v(-87.56, -241.5) * mm});
            skLineSegment(sketch, "E276.top", {"start": v(-90.56, -219.69) * mm, "end": v(-87.6, -219.69) * mm});
            skLineSegment(sketch, "E276.left", {"start": v(-90.56, -208.49) * mm, "end": v(-90.56, -219.69) * mm});
            skLineSegment(sketch, "E276.right", {"start": v(-87.6, -210.65) * mm, "end": v(-87.6, -219.69) * mm});
            skLineSegment(sketch, "E277", {"start": v(-90.54, -241.5) * mm, "end": v(-96.32, -241.5) * mm});
            skLineSegment(sketch, "E278", {"start": v(-96.32, -241.5) * mm, "end": v(-94.39, -238.05) * mm});
            skLineSegment(sketch, "E279", {"start": v(-94.39, -238.05) * mm, "end": v(-94.39, -211.79) * mm});
            skLineSegment(sketch, "E280", {"start": v(-94.39, -211.79) * mm, "end": v(-96.12, -208.49) * mm});
            skLineSegment(sketch, "E281", {"start": v(-96.12, -208.49) * mm, "end": v(-90.56, -208.49) * mm});
            skLineSegment(sketch, "E282", {"start": v(-87.6, -210.65) * mm, "end": v(-81.83, -210.65) * mm});
            skLineSegment(sketch, "E283", {"start": v(-81.83, -210.65) * mm, "end": v(-83.83, -214.26) * mm});
            skLineSegment(sketch, "E284", {"start": v(-83.83, -214.26) * mm, "end": v(-83.83, -219.98) * mm});
            skLineSegment(sketch, "E285", {"start": v(-87.56, -241.5) * mm, "end": v(-81.91, -241.5) * mm});
            skLineSegment(sketch, "E286", {"start": v(-81.91, -241.5) * mm, "end": v(-83.83, -237.83) * mm});
            skLineSegment(sketch, "E287", {"start": v(-83.83, -237.83) * mm, "end": v(-83.83, -223.2) * mm});
            skArc(sketch, "E288", {"start": v(-85.96, -221.28) * mm, "mid": v(-84.7, -220.95) * mm, "end": v(-83.83, -219.98) * mm});
            skArc(sketch, "E289", {"start": v(-83.83, -223.2) * mm, "mid": v(-84.49, -221.83) * mm, "end": v(-85.96, -221.48) * mm});
            skLineSegment(sketch, "E290", {"start": v(-85.96, -221.28) * mm, "end": v(-85.96, -221.48) * mm});
            skLineSegment(sketch, "E291", {"start": v(-70.72, -210.62) * mm, "end": v(-70.72, -217.42) * mm});
            skLineSegment(sketch, "E292", {"start": v(-70.72, -217.42) * mm, "end": v(-74.65, -213.97) * mm});
            skLineSegment(sketch, "E293", {"start": v(-74.65, -213.97) * mm, "end": v(-76.58, -213.97) * mm});
            skLineSegment(sketch, "E294", {"start": v(-76.58, -213.97) * mm, "end": v(-76.58, -217.5) * mm});
            skLineSegment(sketch, "E295", {"start": v(-76.58, -217.5) * mm, "end": v(-72.65, -217.5) * mm});
            skLineSegment(sketch, "E296", {"start": v(-70.72, -219.18) * mm, "end": v(-70.72, -239.68) * mm});
            skLineSegment(sketch, "E297", {"start": v(-72.44, -241.5) * mm, "end": v(-80.5, -241.5) * mm});
            skLineSegment(sketch, "E298", {"start": v(-80.5, -241.5) * mm, "end": v(-80.5, -233.86) * mm});
            skLineSegment(sketch, "E299", {"start": v(-80.5, -233.86) * mm, "end": v(-76.6, -238) * mm});
            skLineSegment(sketch, "E300", {"start": v(-76.6, -238) * mm, "end": v(-74.65, -238) * mm});
            skLineSegment(sketch, "E301", {"start": v(-74.65, -238) * mm, "end": v(-74.65, -220.83) * mm});
            skLineSegment(sketch, "E302", {"start": v(-74.65, -220.83) * mm, "end": v(-78.65, -220.83) * mm});
            skLineSegment(sketch, "E303", {"start": v(-80.52, -218.52) * mm, "end": v(-80.52, -212.44) * mm});
            skLineSegment(sketch, "E304", {"start": v(-70.72, -210.62) * mm, "end": v(-78.44, -210.62) * mm});
            skArc(sketch, "E305", {"start": v(-78.44, -210.62) * mm, "mid": v(-79.82, -211.14) * mm, "end": v(-80.52, -212.44) * mm});
            skArc(sketch, "E306", {"start": v(-80.52, -218.52) * mm, "mid": v(-79.99, -220) * mm, "end": v(-78.65, -220.83) * mm});
            skArc(sketch, "E307", {"start": v(-70.72, -219.18) * mm, "mid": v(-71.3, -217.9) * mm, "end": v(-72.65, -217.5) * mm});
            skArc(sketch, "E308", {"start": v(-72.44, -241.5) * mm, "mid": v(-71.22, -240.93) * mm, "end": v(-70.72, -239.68) * mm});
            skFitSpline(sketch, "E309", {"points": [v(-152.42, -120.98) * mm, v(-139.49, -124.6) * mm, v(-122.6, -123.4) * mm, v(-109.14, -119.91) * mm, v(-94.9, -118.38) * mm, v(-78.33, -120.81) * mm], "startDerivative": vector(79.06, -22.21) * mm, "endDerivative": vector(78.5, -14.75) * mm});
            skFitSpline(sketch, "E310", {"points": [v(-78.33, -120.81) * mm, v(-85.78, -124.39) * mm, v(-97.3, -132.72) * mm], "startDerivative": vector(-16.55, -6.88) * mm, "endDerivative": vector(-21.2, -16.5) * mm});
            skFitSpline(sketch, "E311", {"points": [v(-97.3, -132.72) * mm, v(-84.95, -144.12) * mm, v(-78.33, -153.4) * mm], "startDerivative": vector(24.68, -20.87) * mm, "endDerivative": vector(12.89, -20.49) * mm});
            skFitSpline(sketch, "E312", {"points": [v(-78.33, -153.4) * mm, v(-86.93, -150.97) * mm, v(-107.47, -151.87) * mm, v(-126.43, -155.65) * mm, v(-142.96, -156.37) * mm, v(-152.5, -153.4) * mm], "startDerivative": vector(-48.13, 18.53) * mm, "endDerivative": vector(-53.64, 20.5) * mm});
            skLineSegment(sketch, "E313", {"start": v(-152.43, -125.39) * mm, "end": v(-152.45, -132.5) * mm});
            skFitSpline(sketch, "E314", {"points": [v(-152.43, -125.39) * mm, v(-132.37, -128.36) * mm, v(-106.7, -123.31) * mm, v(-91.66, -121.96) * mm, v(-83.22, -122.99) * mm], "startDerivative": vector(41.85, -22.44) * mm, "endDerivative": vector(45.36, -7.33) * mm});
            skFitSpline(sketch, "E315", {"points": [v(-152.45, -132.5) * mm, v(-132.37, -136.38) * mm, v(-106.88, -131.15) * mm, v(-92.57, -129.07) * mm], "startDerivative": vector(28.9, -20.43) * mm, "endDerivative": vector(40.09, 4.16) * mm});
            skFitSpline(sketch, "E316", {"points": [v(-152.47, -140.43) * mm, v(-143.18, -143.5) * mm, v(-130.21, -143.67) * mm, v(-101.3, -137.28) * mm, v(-93.3, -136.13) * mm], "startDerivative": vector(44.32, -16.94) * mm, "endDerivative": vector(33.66, 2.92) * mm});
            skFitSpline(sketch, "E317", {"points": [v(-152.5, -148.35) * mm, v(-140.12, -151.87) * mm, v(-124.18, -150.25) * mm, v(-95.35, -144.75) * mm, v(-83.87, -145.4) * mm], "startDerivative": vector(49.9, -22.62) * mm, "endDerivative": vector(53.57, -6.12) * mm});
            skLineSegment(sketch, "E318", {"start": v(-152.42, -120.98) * mm, "end": v(-152.42, -117.91) * mm});
            skLineSegment(sketch, "E319", {"start": v(-152.42, -117.91) * mm, "end": v(-156.51, -117.9) * mm});
            skLineSegment(sketch, "E320", {"start": v(-156.51, -117.9) * mm, "end": v(-156.51, -127.44) * mm});
            skLineSegment(sketch, "E321", {"start": v(-156.51, -127.44) * mm, "end": v(-160.03, -127.43) * mm});
            skLineSegment(sketch, "E322", {"start": v(-160.03, -127.43) * mm, "end": v(-160.03, -117.64) * mm});
            skLineSegment(sketch, "E323", {"start": v(-160.03, -117.64) * mm, "end": v(-167.23, -117.62) * mm});
            skLineSegment(sketch, "E324", {"start": v(-167.23, -117.62) * mm, "end": v(-167.23, -128.51) * mm});
            skLineSegment(sketch, "E325", {"start": v(-167.23, -128.51) * mm, "end": v(-170.43, -128.5) * mm});
            skLineSegment(sketch, "E326", {"start": v(-170.43, -128.5) * mm, "end": v(-170.43, -117.83) * mm});
            skLineSegment(sketch, "E327", {"start": v(-170.43, -117.83) * mm, "end": v(-183.39, -117.8) * mm});
            skLineSegment(sketch, "E328", {"start": v(-183.39, -117.8) * mm, "end": v(-183.44, -128.99) * mm});
            skLineSegment(sketch, "E329", {"start": v(-183.44, -128.99) * mm, "end": v(-187.05, -128.98) * mm});
            skLineSegment(sketch, "E330", {"start": v(-187.05, -128.98) * mm, "end": v(-187.05, -118.09) * mm});
            skLineSegment(sketch, "E331", {"start": v(-187.05, -118.09) * mm, "end": v(-193.8, -118.09) * mm});
            skLineSegment(sketch, "E332", {"start": v(-193.8, -118.09) * mm, "end": v(-193.8, -127.44) * mm});
            skLineSegment(sketch, "E333", {"start": v(-193.8, -127.44) * mm, "end": v(-196.77, -127.43) * mm});
            skLineSegment(sketch, "E334", {"start": v(-196.77, -127.43) * mm, "end": v(-196.77, -118.09) * mm});
            skLineSegment(sketch, "E335", {"start": v(-196.77, -118.09) * mm, "end": v(-201.5, -118.09) * mm});
            skLineSegment(sketch, "E336", {"start": v(-201.5, -118.09) * mm, "end": v(-201.2, -153.4) * mm});
            skLineSegment(sketch, "E337", {"start": v(-201.2, -153.4) * mm, "end": v(-176.65, -167.07) * mm});
            skLineSegment(sketch, "E338", {"start": v(-174.6, -165.92) * mm, "end": v(-152.5, -153.4) * mm});
            skLineSegment(sketch, "E339", {"start": v(-176.65, -167.07) * mm, "end": v(-176.65, -129.43) * mm});
            skLineSegment(sketch, "E340", {"start": v(-176.65, -129.43) * mm, "end": v(-174.6, -129.43) * mm});
            skLineSegment(sketch, "E341", {"start": v(-174.6, -129.43) * mm, "end": v(-174.6, -165.92) * mm});
            skLineSegment(sketch, "E342", {"start": v(-196.1, -151.02) * mm, "end": v(-185.47, -156.94) * mm});
            skLineSegment(sketch, "E343", {"start": v(-168.72, -139.68) * mm, "end": v(-168.72, -155.86) * mm});
            skLineSegment(sketch, "E344", {"start": v(-168.72, -155.86) * mm, "end": v(-158.45, -151.18) * mm});
            skLineSegment(sketch, "E345", {"start": v(-158.45, -151.18) * mm, "end": v(-158.45, -138.96) * mm});
            skLineSegment(sketch, "E346", {"start": v(-196.1, -151.02) * mm, "end": v(-196.1, -138.61) * mm});
            skLineSegment(sketch, "E347", {"start": v(-185.47, -156.94) * mm, "end": v(-185.47, -139.7) * mm});
            skArc(sketch, "E348", {"start": v(-185.47, -139.7) * mm, "mid": v(-190.19, -133.27) * mm, "end": v(-196.1, -138.61) * mm});
            skArc(sketch, "E349", {"start": v(-158.45, -138.96) * mm, "mid": v(-163.97, -133.82) * mm, "end": v(-168.72, -139.68) * mm});
            skLineSegment(sketch, "E350.trimOffspring", {"start": v(-152.47, -140.43) * mm, "end": v(-152.5, -148.35) * mm});
            skText(sketch, "E351", { "text": "2014", "fontName": "OpenSans-Regular.ttf"});
            skText(sketch, "E352", { "text": "2015", "fontName": "OpenSans-Bold.ttf"});
            skText(sketch, "E353", { "text": "2017", "fontName": "OpenSans-Bold.ttf"});
            skText(sketch, "E354", { "text": "2016", "fontName": "OpenSans-Bold.ttf"});
            const initialGuessF2  = {"E351": [-0.36886, -0.18459, 1, 0, 0.01905], "E352": [-0.37257, -0.27609, 1, 0, 0.01905], "E353": [-0.17199, -0.27507, 1, 0, 0.01905], "E354": [-0.20443, -0.19509, 1, 0, 0.01905]};
            skSetInitialGuess(sketch, initialGuessF2);
            skSolve(sketch);
        }
        {
            var Q0;
            Q0 = qSketchRegion(id + "F2", true);
            extrude(context, id + "F3", {"entities" : qUnion([Q0]), "operationType" : NewBodyOperationType.REMOVE, "oppositeDirection" : true, "depth" : 2.54 * mm, "offsetDistance" : 25.4 * mm});
        }
        {
            var Q0;
            {var subQ0=sQuery(id+"F0.wireOp",EDGE,"E0");var subQ1=sQuery(id+"F0.wireOp",EDGE,"E3");var subQ2=sQuery(id+"F0.wireOp",EDGE,"E1");var subQ3=sQuery(id+"F0.wireOp",EDGE,"E2");Q0=makeQuery(id+"F3.boolean.opBoolean","SPLIT",FACE,{"disambiguationData":[TD([makeQuery(id+"F1.opExtrude","SWEPT_FACE",FACE,{"disambiguationData":[OSD([subQ0])]})])],"derivedFrom":makeQuery(id+"F1.opExtrude","CAP_FACE",FACE,{"disambiguationData":[OSD([subQ0,subQ2,subQ3,subQ1])],"isStart":false})});}
            var sketch = newSketch(context, id + "F4", { "sketchPlane" : qUnion([Q0])});
            skText(sketch, "E355", { "text": "Thank you", "fontName": "AllertaStencil-Regular.ttf"});
            skText(sketch, "E356", { "text": "for your dedication ", "fontName": "AllertaStencil-Regular.ttf"});
            skPoint(sketch, "E357", {"position": v(-228.6, -279.4) * mm});
            skLineSegment(sketch, "E358", {"start": v(-228.6, -279.4) * mm, "end": v(-228.6, -171.45) * mm, "construction": true});
            skLineSegment(sketch, "E359", {"start": v(-228.6, -107.95) * mm, "end": v(-228.6, 0) * mm, "construction": true});
            const initialGuessF4  = {"E355": [-0.32023, -0.03886, 1, 0, 0.0254], "E356": [-0.40008, -0.07696, 1, 0, 0.0254]};
            skSetInitialGuess(sketch, initialGuessF4);
            skSolve(sketch);
        }
        {
            var Q0;
            Q0 = qSketchRegion(id + "F4", true);
            extrude(context, id + "F5", {"entities" : qUnion([Q0]), "operationType" : NewBodyOperationType.REMOVE, "oppositeDirection" : true, "depth" : 2.54 * mm, "offsetDistance" : 25.4 * mm});
        }
    });
